# Revit family: Titus CBAL2-24 Wide, Linear Chilled Beam, Face Hosted, Revit 2020, R1.4
name_source: partatom
category: Mechanical Equipment
units: mm (PartAtom-declared; Revit-internal decimal feet)

## family parameters
Cut with Voids When Loaded = Yes
Host = Face
OmniClass Number = 23.75.70.17.31
OmniClass Title = Induction Units
Part Type = Normal
Room Calculation Point = No
Round Connector Dimension = Use Radius
Shared = No

## types (2) — shared parameters
1/2" In MNPT = No
1/2" in Sweat = Yes
10 Feet = No
10" Oval = No
2-Pipe System = No
24" Wide Beam = Yes
26 - White = Yes
2P1C - 2 Pipe, 1 Coil Circuit = No
2P2C - 2 Pipe, 2 Coil Circuit = No
3 Feet = No
3/4" In MNPT = No
4-Pipe System = Yes
5 Feet = No
5" Dia. = No
6 Feet = No
7 Feet = No
8 Feet = No
8" Oval = No
84 - Black = No
9 Feet = No
Actual Cooling Entering Dry Bulb Temperature = 0 °F
Actual Cooling Entering Wet Bulb Temperature = 0 °F
Actual Cooling Leaving Dry Bulb Temperature = 0 °F
Actual Cooling Leaving Wet Bulb Temperature = 0 °F
Actual External Static Pressure = 0.00 in-wg
Actual Heating Entering Dry Bulb Temperature = 0 °F
Actual Heating Leaving Dry Bulb Temperature = 0 °F
Actual Height = 8 3/8"
Actual Oval Width = 9 3/8"
Actual Oval height = 5 1/4"
Actual Total Static Pressure = 0.00 in-wg
B - One-way, Back = No
CTRL Multi-Inlet Angle = 90.00°
CTRL Multi-Inlet Round Angle = 90.00°
CTRL Oval Connector Offset = 4"
CTRL Perforation Hole Dia = 1/8"
CTRL Perforation Offset = 1/2"
CTRL Round Connector Offset = 0"
CTRL Thickness = 1/16"
CWR Outlet Description = CWR-Outlet
CWS Inlet Description = CWS Inlet
Coil Material = Metal - Copper
Condenser Inlet Radius = 1/4"
Condenser Outlet Radius = 1/4"
Condenser Pressure Drop = 0.00 psi
Conditioned Air (Oval) Description = Disabled
Conditioned Air (Round) Description = Conditioned Air
Conditioned Air Connection Height = 1/2"
Conditioned Air Connection Width = 1/2"
Description = Linear Chilled Beam Diffuser, Ceiling Mounted
Design Ambient Summer Dry Bulb Temperature = 0 °F
Design Ambient Winter Dry Bulb Temperature = 0 °F
Design Ambient summer Wet bulb Temperature = 0 °F
Design Cooling Minimum Air Flow = 0 CFM
Design Heating Maximum Air Flow = 0 CFM
Design Heating Minimum Air Flow = 0 CFM
Design cooling Maximum Air Flow = 0 CFM
Evaporator Inlet Radius = 1/4"
Evaporator Outlet Radius = 1/4"
Evaporator Pressure Drop = 0.00 psi
Frame Extension = 3/8"
Front Arrow = Yes
G = 4"
H12 - SS Flex Hose - 12in = No
H18 - SS Flex Hose - 18in = No
H24 - SS Flex Hose - 24in = No
HWR Description = HWR Outlet
HWS Inlet Description = HWS Inlet
Hanger Visibility = No
Height = 10 1/8"
Hor Chilled Water Return Offset = 7 1/8"
Hor Chilled Water Supply Offset = 7 3/4"
Hor Hot Water Return Offset = 2 1/2"
Hor Hot Water Supply Offset = 2 1/2"
Inner Width = 23 3/8"
Input your Special Finish's name = Input your Special Finish's name
Lay In Width = 23 3/4"
M13 = Yes
M17 = No
M19 = No
M23 = No
M27 = No
M31 = No
Manufacturer = Titus HVAC
Material = Galvanized G90
Model = CBAL2-24
Pipe Connections Left Hand = No
Pipe Connections Right Hand = Yes
Pipe Height = 6"
Primary Air Extension = 2 5/8"
Primary Air Ver Offset = 6 1/8"
Select a Piping Connection Type = 1
Select a Water Coil Connection = 2
Select an Air Nozzle Configuration = 1
Select an Exposed Face Finish = 1
Show Oval Connector = No
Show Room Tag = No
Show Round Connector = Yes
Side Plate = Yes
Top Middle = No
zero-valued in all types: Actual Coefficient of Performance, Actual Energy Efficiency Rating (BTU/h.W), Actual Filter Face Area, Actual Full Load Efficiency

## per-type parameters (varying)
- CBAL2-24 LAY-IN: 2 - Two-way,Throw=Yes; 2 Feet=No; 3 - LAY-IN=Yes; 4 Feet=Yes; 4" Dia.=No; 4P1C - 4 Pipe, 1 Coil Circuit=No; 4P2C - 4 Pipe, 2 Coil Circuit=Yes; 6" Dia.=Yes; Actual Radius=2 15/16"; Back Arrow=Yes; CTRL Angle=0.00°; CTRL Multi-Inlet Connector Offset=8 7/8"; CTRL Multi-Inlet Offset=5"; CTRL Multi-Inlet Oval Angle=90.00°; CTRL Multi-Inlet Oval Connector Offset=8 7/8"; CTRL Multi-Inlet Round Connector Offset=8 7/8"; CTRL Offset=0"; CTRL Pipe Connector Offset=46 5/64"; CWR Ver Offset=7 1/8"; CWS Ver Offset=7 7/8"; Conditioned Air Connection Radius=3"; Connector Offset=8 7/8"; Default Elevation=2"; F=6 7/8"; F - One-way, Front=No; HWR Ver Offset=9 5/8"; HWS Ver Offset=10 3/8"; Hanger Dimension F=6 7/8"; Inner Length=47 3/8"; Layin depath=5/16"; Multi-Inlet=No; NT - Tegular 9/16 Inch=No; Select Border Type=1; Select a Beam Length=3; Select a Water-Coil Type=6; Select an Air Inlet Dia=3; Select an Air Inlet Location=1; Select an Air Throw Pattern=1; Side Middle=Yes; Top Plate=No; Total Length=47 3/4"; Total Width=23 3/4"
- CBAL2-24 NT Border Type: 2 - Two-way,Throw=No; 2 Feet=Yes; 3 - LAY-IN=No; 4 Feet=No; 4" Dia.=Yes; 4P1C - 4 Pipe, 1 Coil Circuit=Yes; 4P2C - 4 Pipe, 2 Coil Circuit=No; 6" Dia.=No; Actual Radius=1 15/16"; Back Arrow=No; CTRL Angle=90.00°; CTRL Multi-Inlet Connector Offset=8 1/2"; CTRL Multi-Inlet Offset=0"; CTRL Multi-Inlet Oval Angle=0.00°; CTRL Multi-Inlet Oval Connector Offset=6 5/64"; CTRL Multi-Inlet Round Connector Offset=8 1/2"; CTRL Offset=7/16"; CTRL Pipe Connector Offset=21 45/64"; CWR Ver Offset=7"; CWS Ver Offset=7 5/8"; Conditioned Air Connection Radius=2"; Connector Offset=6 5/64"; Default Elevation=0"; F=4 1/2"; F - One-way, Front=Yes; HWR Ver Offset=9 1/2"; HWS Ver Offset=10 1/8"; Hanger Dimension F=4 5/16"; Inner Length=23"; Layin depath=3/8"; Multi-Inlet=Yes; NT - Tegular 9/16 Inch=Yes; Select Border Type=2; Select a Beam Length=1; Select a Water-Coil Type=2; Select an Air Inlet Dia=1; Select an Air Inlet Location=4; Select an Air Throw Pattern=2; Side Middle=No; Top Plate=Yes; Total Length=23 3/8"; Total Width=23 3/8"

## geometry (parser evidence)
native form markers: Sweep x26
no freeform markers — native parametric forms only
